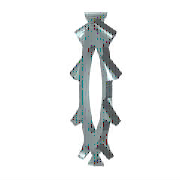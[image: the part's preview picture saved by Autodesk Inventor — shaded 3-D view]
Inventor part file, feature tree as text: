
AUTODESK INVENTOR PART (.ipt)
format: ipt  version: 2015 (Build 190159000, 159)  size: 158,720 bytes
history: native  units: mm (DEFAULTED — no unit token found)
features: sketch x2, extrude x1, pattern_circular x1, other x1, plane x1
ambient origin geometry x7: Origin, YZ Plane, XY Plane, X Axis, Y Axis, Z Axis, Center Point
bodies: Solid1 (feature_tree), Body (feature_tree)
feature tree (6):
  extrude  "Cut"  Depth=3.5814mm
  pattern_circular  "Cuts"  [2 undecoded]
  other  "Work Axis1"
  plane  "Work Plane1"
  sketch  "Sketch1"  dims[d0=8.128mm d1=3.5814mm]
  sketch  "Sketch2"  dims[d2=0.5588mm d3=0.0mm d4=30.0deg d5=5.8547mm d6=0.5588mm d7=0.0mm d8=0.12192mm d9=60.0mm d11=360.0deg d12=0.0mm d13=0.0mm d14=0.0mm d15=0.0mm d16=90.0deg]
note: 2 required parameter values undecoded (feature->parameter linkage not recoverable at this tier; creation-order binding heuristic only, values carry confidence <= 0.55)
